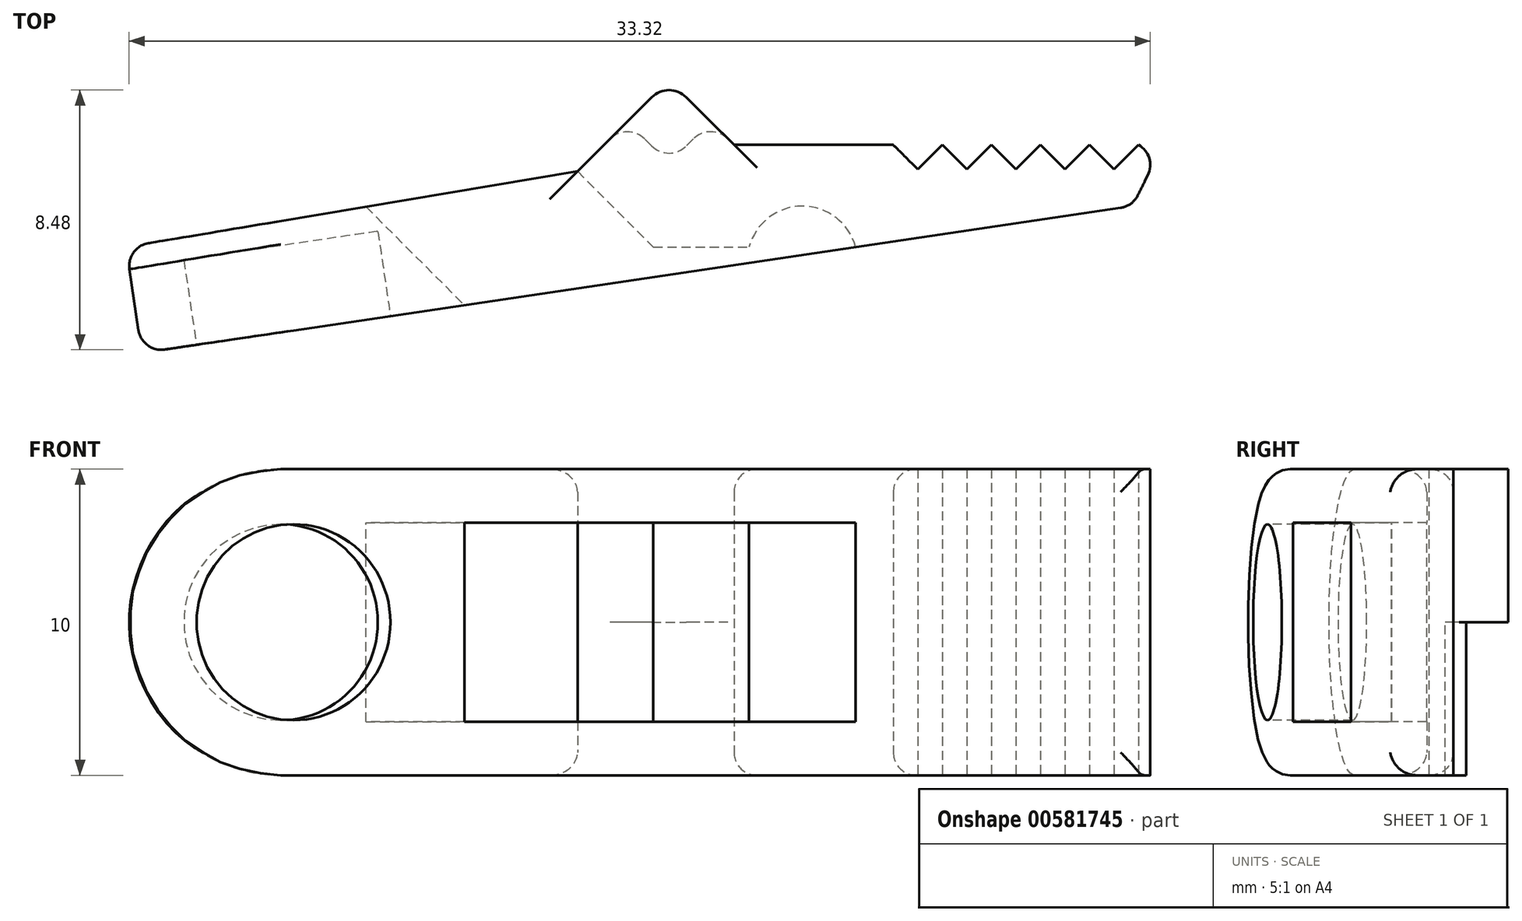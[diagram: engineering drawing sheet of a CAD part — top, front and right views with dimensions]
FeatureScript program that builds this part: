
annotation { "Feature Type Name" : "Feature", "Feature Type Description" : "" }
export const myFeature = defineFeature(function(context is Context, id is Id, definition is map)
    precondition{}
    {
        {
            var Q0;
            Q0=qCreatedBy(makeId("Top.planeOp"),FACE);
            var sketch = newSketch(context, id + "F0", { "sketchPlane" : qUnion([Q0])});
            skLineSegment(sketch, "E0", {"start": v(0, -4.1) * mm, "end": v(-1.2, -2.9) * mm, "construction": true});
            skLineSegment(sketch, "E1", {"start": v(-1.2, -2.9) * mm, "end": v(-5, -4.9) * mm, "construction": true});
            skLineSegment(sketch, "E2", {"start": v(-5, -4.9) * mm, "end": v(-10.2, -4.9) * mm, "construction": true});
            skLineSegment(sketch, "E3", {"start": v(-10.2, -4.9) * mm, "end": v(-10.2, 0) * mm, "construction": true});
            skLineSegment(sketch, "E4", {"start": v(-10.2, 0) * mm, "end": v(0, 0) * mm, "construction": true});
            skLineSegment(sketch, "E5.MirrorCS", {"start": v(0, 4.1) * mm, "end": v(-1.2, 2.9) * mm, "construction": true});
            skLineSegment(sketch, "E6.MirrorCS", {"start": v(-10.2, 4.9) * mm, "end": v(-10.2, 0) * mm, "construction": true});
            skLineSegment(sketch, "E7.MirrorCS", {"start": v(-5, 4.9) * mm, "end": v(-10.2, 4.9) * mm, "construction": true});
            skLineSegment(sketch, "E8.MirrorCS", {"start": v(-1.2, 2.9) * mm, "end": v(-5, 4.9) * mm, "construction": true});
            skLineSegment(sketch, "E9", {"start": v(0, -4.1) * mm, "end": v(-3.48, -4.1) * mm, "construction": true});
            skSolve(sketch);
        }
        {
            var Q0;
            Q0=qCreatedBy(makeId("Top.planeOp"),FACE);
            var sketch = newSketch(context, id + "F1", { "sketchPlane" : qUnion([Q0])});
            skArc(sketch, "E10", {"start": v(0, -4.1) * mm, "mid": v(-1.74, -2.76) * mm, "end": v(-3.48, -4.1) * mm});
            skLineSegment(sketch, "E11", {"start": v(-3.97, -0.76) * mm, "end": v(10.03, -0.76) * mm});
            skLineSegment(sketch, "E12", {"start": v(10.03, -0.76) * mm, "end": v(9.03, -2.76) * mm});
            skLineSegment(sketch, "E13", {"start": v(-3.97, -0.76) * mm, "end": v(-6.1, 1.36) * mm});
            skLineSegment(sketch, "E14", {"start": v(-6.1, 1.36) * mm, "end": v(-9.08, -1.63) * mm});
            skLineSegment(sketch, "E15", {"start": v(-9.08, -1.63) * mm, "end": v(-23.87, -4.1) * mm});
            skLineSegment(sketch, "E16", {"start": v(-23.87, -4.1) * mm, "end": v(-23.3, -7.55) * mm});
            skLineSegment(sketch, "E17", {"start": v(9.03, -2.76) * mm, "end": v(-23.3, -7.55) * mm});
            skLineSegment(sketch, "E18", {"start": v(-9.08, -1.63) * mm, "end": v(-6.6, -4.1) * mm});
            skLineSegment(sketch, "E19", {"start": v(-6.6, -4.1) * mm, "end": v(-3.48, -4.1) * mm});
            skLineSegment(sketch, "E20", {"start": v(-15.98, -2.78) * mm, "end": v(-12.77, -6) * mm});
            skLineSegment(sketch, "E21.MirrorCS", {"start": v(-9.08, 1.63) * mm, "end": v(-6.6, 4.1) * mm});
            skLineSegment(sketch, "E22.MirrorCS", {"start": v(-3.97, 0.76) * mm, "end": v(-6.1, -1.36) * mm});
            skLineSegment(sketch, "E23.MirrorCS", {"start": v(-23.87, 4.1) * mm, "end": v(-23.3, 7.55) * mm});
            skLineSegment(sketch, "E24.MirrorCS", {"start": v(-6.6, 4.1) * mm, "end": v(-3.48, 4.1) * mm});
            skLineSegment(sketch, "E25.MirrorCS", {"start": v(9.03, 2.76) * mm, "end": v(-23.3, 7.55) * mm});
            skLineSegment(sketch, "E26.MirrorCS", {"start": v(10.03, 0.76) * mm, "end": v(9.03, 2.76) * mm});
            skLineSegment(sketch, "E27.MirrorCS", {"start": v(-15.98, 2.78) * mm, "end": v(-12.77, 6) * mm});
            skArc(sketch, "E28.MirrorCS", {"start": v(0, 4.1) * mm, "mid": v(-1.74, 2.76) * mm, "end": v(-3.48, 4.1) * mm});
            skLineSegment(sketch, "E29.MirrorCS", {"start": v(-3.97, 0.76) * mm, "end": v(10.03, 0.76) * mm});
            skLineSegment(sketch, "E30.MirrorCS", {"start": v(-9.08, 1.63) * mm, "end": v(-23.87, 4.1) * mm});
            skLineSegment(sketch, "E31.MirrorCS", {"start": v(-6.1, -1.36) * mm, "end": v(-9.08, 1.63) * mm});
            skLineSegment(sketch, "E32", {"start": v(9.23, -0.76) * mm, "end": v(8.43, -1.56) * mm});
            skLineSegment(sketch, "E33", {"start": v(8.43, -1.56) * mm, "end": v(7.63, -0.76) * mm});
            skLineSegment(sketch, "E34.1.0.0", {"start": v(6.83, -1.56) * mm, "end": v(6.03, -0.76) * mm});
            skLineSegment(sketch, "E34.1.0.1", {"start": v(7.63, -0.76) * mm, "end": v(6.83, -1.56) * mm});
            skLineSegment(sketch, "E34.2.0.0", {"start": v(5.23, -1.56) * mm, "end": v(4.43, -0.76) * mm});
            skLineSegment(sketch, "E34.2.0.1", {"start": v(6.03, -0.76) * mm, "end": v(5.23, -1.56) * mm});
            skLineSegment(sketch, "E34.direction1", {"start": v(8.43, -1.56) * mm, "end": v(6.83, -1.56) * mm, "construction": true});
            skLineSegment(sketch, "E35.0.3.0", {"start": v(3.63, -1.56) * mm, "end": v(2.83, -0.76) * mm});
            skLineSegment(sketch, "E35.3.3.0", {"start": v(4.43, -0.76) * mm, "end": v(3.63, -1.56) * mm});
            skLineSegment(sketch, "E36.0.4.0", {"start": v(2.03, -1.56) * mm, "end": v(1.23, -0.76) * mm});
            skLineSegment(sketch, "E36.3.4.0", {"start": v(2.83, -0.76) * mm, "end": v(2.03, -1.56) * mm});
            skSolve(sketch);
        }
        {
            var Q0;
            {var subQ0=sQuery(id+"F1.wireOp",EDGE,"E16");Q0=makeQuery(id+"F1.imprint","IMPRINT",FACE,{"disambiguationData":[TD([[makeQuery(id+"F1.imprint","IMPRINT",EDGE,{"derivedFrom":subQ0}),1.0]])]});}
            var Q1;
            {var subQ1=sQuery(id+"F1.wireOp",EDGE,"E10");Q1=makeQuery(id+"F1.imprint","IMPRINT",FACE,{"disambiguationData":[TD([[makeQuery(id+"F1.imprint","IMPRINT",EDGE,{"derivedFrom":subQ1}),1.0]])]});}
            var Q2;
            {var subQ1=sQuery(id+"F1.wireOp",EDGE,"E10");Q2=makeQuery(id+"F1.imprint","IMPRINT",FACE,{"disambiguationData":[TD([[makeQuery(id+"F1.imprint","IMPRINT",EDGE,{"derivedFrom":subQ1}),-1.0]])]});}
            extrude(context, id + "F2", {"entities" : qUnion([Q0, Q1, Q2]), "endBound" : BoundingType.SYMMETRIC, "depth" : 10 * mm, "offsetDistance" : 25 * mm});
        }
        {
            var Q0;
            {var subQ1=sQuery(id+"F1.wireOp",EDGE,"E10");Q0=makeQuery(id+"F1.imprint","IMPRINT",FACE,{"disambiguationData":[TD([[makeQuery(id+"F1.imprint","IMPRINT",EDGE,{"derivedFrom":subQ1}),1.0]])]});}
            extrude(context, id + "F3", {"entities" : qUnion([Q0]), "operationType" : NewBodyOperationType.REMOVE, "endBound" : BoundingType.SYMMETRIC, "oppositeDirection" : true, "depth" : 6.5 * mm, "offsetDistance" : 25 * mm});
        }
        {
            var Q0;
            {var subQ0=sQuery(id+"F1.wireOp",EDGE,"E14");var subQ1=sQuery(id+"F1.wireOp",EDGE,"E13");var subQ2=makeQuery(id+"F1.imprint","INTERSECT",VERTEX,{"derivedFrom":[subQ1,subQ0]});Q0=makeQuery(id+"F1.imprint","IMPRINT",FACE,{"disambiguationData":[TD([[makeQuery(id+"F1.imprint","IMPRINT",EDGE,{"disambiguationData":[TD([[subQ2,1.0]])],"derivedFrom":subQ1}),1.0]])]});}
            var Q1;
            Q1=makeQuery(id+"F2.opExtrude","CAP_FACE",FACE,{"disambiguationData":[OSD([sQuery(id+"F1.wireOp",EDGE,"E11"),sQuery(id+"F1.wireOp",EDGE,"E12"),sQuery(id+"F1.wireOp",EDGE,"E13"),sQuery(id+"F1.wireOp",EDGE,"E14"),sQuery(id+"F1.wireOp",EDGE,"E15"),sQuery(id+"F1.wireOp",EDGE,"E16"),sQuery(id+"F1.wireOp",EDGE,"E17"),sQuery(id+"F1.wireOp",EDGE,"E22.MirrorCS"),sQuery(id+"F1.wireOp",EDGE,"E31.MirrorCS")])],"isStart":false});
            extrude(context, id + "F4", {"entities" : qUnion([Q0]), "operationType" : NewBodyOperationType.ADD, "endBound" : BoundingType.UP_TO_SURFACE, "depth" : 25 * mm, "endBoundEntityFace" : qUnion([Q1]), "offsetDistance" : 25 * mm});
        }
        {
            var Q0;
            Q0=makeQuery(id+"F2.opExtrude","SWEPT_FACE",FACE,{"disambiguationData":[OSD([sQuery(id+"F1.wireOp",EDGE,"E17")])]});
            var sketch = newSketch(context, id + "F5", { "sketchPlane" : qUnion([Q0])});
            skCircle(sketch, "E37", {"center": v(-19.15, 0) * mm, "radius": 3.2 * mm});
            skCircle(sketch, "E38", {"center": v(-19.15, 0) * mm, "radius": 5 * mm});
            skSolve(sketch);
        }
        {
            var Q0;
            {var subQ0=sQuery(id+"F5.wireOp",EDGE,"E38");var subQ1=sQuery(id+"F1.wireOp",EDGE,"E17");var subQ4=makeQuery(id+"F2.opExtrude","CAP_EDGE",EDGE,{"disambiguationData":[OSD([subQ1])],"isStart":false});var subQ5=makeQuery(id+"F5.imprint","INTERSECT",VERTEX,{"derivedFrom":[subQ4,subQ0]});Q0=makeQuery(id+"F5.imprint","IMPRINT",FACE,{"disambiguationData":[TD([[makeQuery(id+"F5.imprint","IMPRINT",EDGE,{"disambiguationData":[TD([[subQ5,-1.0]])],"derivedFrom":subQ0}),-1.0]])]});}
            var Q1;
            {var subQ0=sQuery(id+"F5.wireOp",EDGE,"E38");var subQ1=sQuery(id+"F1.wireOp",EDGE,"E17");var subQ4=makeQuery(id+"F2.opExtrude","CAP_EDGE",EDGE,{"disambiguationData":[OSD([subQ1])],"isStart":true});var subQ5=makeQuery(id+"F5.imprint","INTERSECT",VERTEX,{"derivedFrom":[subQ4,subQ0]});Q1=makeQuery(id+"F5.imprint","IMPRINT",FACE,{"disambiguationData":[TD([[makeQuery(id+"F5.imprint","IMPRINT",EDGE,{"disambiguationData":[TD([[subQ5,1.0]])],"derivedFrom":subQ0}),-1.0]])]});}
            var Q2;
            Q2=makeQuery(id+"F2.opExtrude","SWEPT_FACE",FACE,{"disambiguationData":[OSD([sQuery(id+"F1.wireOp",EDGE,"E16")])]});
            extrude(context, id + "F6", {"entities" : qUnion([Q0, Q1, Q2]), "operationType" : NewBodyOperationType.REMOVE, "endBound" : BoundingType.UP_TO_NEXT, "oppositeDirection" : true, "depth" : 25 * mm, "offsetDistance" : 25 * mm});
        }
        {
            var Q0;
            Q0=makeQuery(id+"F5.imprint","IMPRINT",FACE,{"disambiguationData":[TD([[makeQuery(id+"F5.imprint","IMPRINT",EDGE,{"derivedFrom":sQuery(id+"F5.wireOp",EDGE,"E37")}),1.0]])]});
            extrude(context, id + "F7", {"entities" : qUnion([Q0]), "operationType" : NewBodyOperationType.REMOVE, "oppositeDirection" : true, "depth" : 2.8 * mm, "offsetDistance" : 25 * mm});
        }
        {
            var Q0;
            Q0=makeQuery(id+"F4.opExtrude","SWEPT_EDGE",EDGE,{"disambiguationData":[OSD([sQuery(id+"F1.wireOp",EDGE,"E13"),sQuery(id+"F1.wireOp",EDGE,"E14")])]});
            var Q1;
            Q1=makeQuery(id+"F2.opExtrude","SWEPT_EDGE",EDGE,{"disambiguationData":[OSD([sQuery(id+"F1.wireOp",EDGE,"E22.MirrorCS"),sQuery(id+"F1.wireOp",EDGE,"E31.MirrorCS")])]});
            var Q2;
            Q2=makeQuery(id+"F2.opExtrude","SWEPT_EDGE",EDGE,{"disambiguationData":[OSD([sQuery(id+"F1.wireOp",EDGE,"E14"),sQuery(id+"F1.wireOp",EDGE,"E31.MirrorCS")])]});
            var Q3;
            Q3=makeQuery(id+"F2.opExtrude","SWEPT_EDGE",EDGE,{"disambiguationData":[OSD([sQuery(id+"F1.wireOp",EDGE,"E13"),sQuery(id+"F1.wireOp",EDGE,"E22.MirrorCS")])]});
            fillet(context, id + "F8", {"entities" : qUnion([Q0, Q1, Q2, Q3]), "radius" : 0.8 * mm, "tangentPropagation" : true, "allowEdgeOverflow" : false});
        }
        {
            var Q0;
            Q0=makeQuery(id+"F2.opExtrude","CAP_EDGE",EDGE,{"disambiguationData":[OSD([sQuery(id+"F1.wireOp",EDGE,"E15")])],"isStart":false});
            var Q1;
            Q1=makeQuery(id+"F2.opExtrude","CAP_EDGE",EDGE,{"disambiguationData":[OSD([sQuery(id+"F1.wireOp",EDGE,"E17")])],"isStart":false});
            var Q2;
            Q2=makeQuery(id+"F2.opExtrude","SWEPT_EDGE",EDGE,{"disambiguationData":[OSD([sQuery(id+"F1.wireOp",EDGE,"E12"),sQuery(id+"F1.wireOp",EDGE,"E17")])]});
            var Q3;
            Q3=makeQuery(id+"F2.opExtrude","SWEPT_EDGE",EDGE,{"disambiguationData":[OSD([sQuery(id+"F1.wireOp",EDGE,"E11"),sQuery(id+"F1.wireOp",EDGE,"E12")])]});
            var Q4;
            {var subQ0=sQuery(id+"F1.wireOp",EDGE,"E11");Q4=makeQuery(id+"F2.opExtrude","CAP_EDGE",EDGE,{"disambiguationData":[OSD([subQ0]),TDD([makeQuery(id+"F1.imprint","IMPRINT",EDGE,{"disambiguationData":[TD([[makeQuery(id+"F1.imprint","INTERSECT",VERTEX,{"derivedFrom":[subQ0,sQuery(id+"F1.wireOp",EDGE,"E13")]}),-1.0]])],"derivedFrom":subQ0})])],"isStart":false});}
            var Q5;
            {var subQ0=sQuery(id+"F1.wireOp",EDGE,"E11");Q5=makeQuery(id+"F2.opExtrude","CAP_EDGE",EDGE,{"disambiguationData":[OSD([subQ0]),TDD([makeQuery(id+"F1.imprint","IMPRINT",EDGE,{"disambiguationData":[TD([[makeQuery(id+"F1.imprint","INTERSECT",VERTEX,{"derivedFrom":[subQ0,sQuery(id+"F1.wireOp",EDGE,"E13")]}),-1.0]])],"derivedFrom":subQ0})])],"isStart":true});}
            fillet(context, id + "F9", {"entities" : qUnion([Q0, Q1, Q2, Q3, Q4, Q5]), "radius" : .75 * mm, "tangentPropagation" : true, "allowEdgeOverflow" : false});
        }
    });
